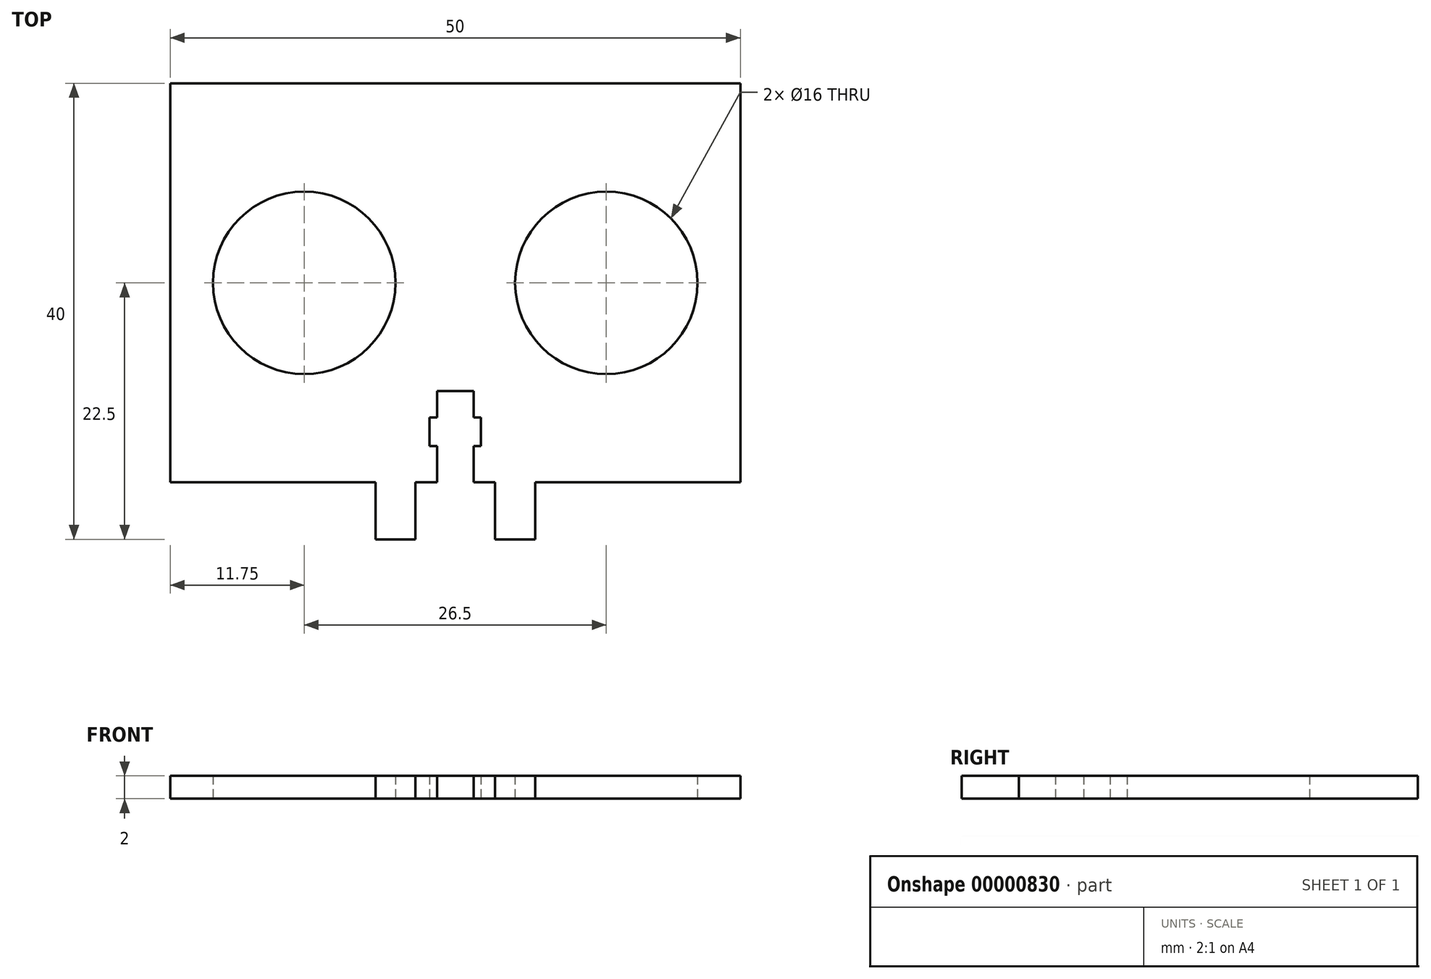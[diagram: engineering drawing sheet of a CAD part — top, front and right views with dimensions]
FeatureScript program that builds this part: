
annotation { "Feature Type Name" : "Feature", "Feature Type Description" : "" }
export const myFeature = defineFeature(function(context is Context, id is Id, definition is map)
    precondition{}
    {
        {
            var Q0;
            Q0=qCreatedBy(makeId("Top.planeOp"),FACE);
            var sketch = newSketch(context, id + "F0", { "sketchPlane" : qUnion([Q0])});
            skLineSegment(sketch, "E0.rect.bottom", {"start": v(25, -17.5) * mm, "end": v(1.6, -17.5) * mm});
            skLineSegment(sketch, "E0.rect.top", {"start": v(25, 17.5) * mm, "end": v(-25, 17.5) * mm});
            skLineSegment(sketch, "E0.rect.left", {"start": v(25, -17.5) * mm, "end": v(25, 17.5) * mm});
            skLineSegment(sketch, "E0.rect.right", {"start": v(-25, -17.5) * mm, "end": v(-25, 17.5) * mm});
            skPoint(sketch, "E0.rect.middle", {"position": v(0, 0) * mm});
            skLineSegment(sketch, "E1", {"start": v(-29.94, 0) * mm, "end": v(40.04, 0) * mm, "construction": true});
            skCircle(sketch, "E2", {"center": v(-13.25, 0) * mm, "radius": 8 * mm});
            skLineSegment(sketch, "E3", {"start": v(0, 12.7) * mm, "end": v(0, -27.18) * mm, "construction": true});
            skCircle(sketch, "E4.0.MirrorC", {"center": v(13.25, 0) * mm, "radius": 8 * mm});
            skLineSegment(sketch, "E5", {"start": v(-7, -17.5) * mm, "end": v(-7, -22.5) * mm});
            skLineSegment(sketch, "E6", {"start": v(-7, -22.5) * mm, "end": v(-3.5, -22.5) * mm});
            skLineSegment(sketch, "E7", {"start": v(-3.5, -22.5) * mm, "end": v(-3.5, -17.5) * mm});
            skLineSegment(sketch, "E8", {"start": v(-3.5, -17.5) * mm, "end": v(-1.6, -17.5) * mm});
            skLineSegment(sketch, "E9", {"start": v(-1.6, -17.5) * mm, "end": v(-1.6, -14.3) * mm});
            skLineSegment(sketch, "E10", {"start": v(-1.6, -14.3) * mm, "end": v(-2.25, -14.3) * mm});
            skLineSegment(sketch, "E11", {"start": v(-2.25, -14.3) * mm, "end": v(-2.25, -11.8) * mm});
            skLineSegment(sketch, "E12", {"start": v(-2.25, -11.8) * mm, "end": v(-1.6, -11.8) * mm});
            skLineSegment(sketch, "E13", {"start": v(-1.6, -11.8) * mm, "end": v(-1.6, -9.5) * mm});
            skLineSegment(sketch, "E14", {"start": v(-1.6, -9.5) * mm, "end": v(0, -9.5) * mm});
            skLineSegment(sketch, "E15.0.MirrorCS", {"start": v(2.25, -11.8) * mm, "end": v(1.6, -11.8) * mm});
            skLineSegment(sketch, "E15.1.MirrorCS", {"start": v(1.6, -14.3) * mm, "end": v(2.25, -14.3) * mm});
            skLineSegment(sketch, "E15.2.MirrorCS", {"start": v(7, -17.5) * mm, "end": v(7, -22.5) * mm});
            skLineSegment(sketch, "E15.3.MirrorCS", {"start": v(3.5, -22.5) * mm, "end": v(3.5, -17.5) * mm});
            skLineSegment(sketch, "E15.4.MirrorCS", {"start": v(7, -22.5) * mm, "end": v(3.5, -22.5) * mm});
            skLineSegment(sketch, "E15.5.MirrorCS", {"start": v(1.6, -17.5) * mm, "end": v(1.6, -14.3) * mm});
            skLineSegment(sketch, "E15.6.MirrorCS", {"start": v(1.6, -9.5) * mm, "end": v(0, -9.5) * mm});
            skLineSegment(sketch, "E15.7.MirrorCS", {"start": v(3.5, -17.5) * mm, "end": v(1.6, -17.5) * mm});
            skLineSegment(sketch, "E15.8.MirrorCS", {"start": v(1.6, -11.8) * mm, "end": v(1.6, -9.5) * mm});
            skLineSegment(sketch, "E15.9.MirrorCS", {"start": v(2.25, -14.3) * mm, "end": v(2.25, -11.8) * mm});
            skLineSegment(sketch, "E16.trimOffspring", {"start": v(-1.6, -17.5) * mm, "end": v(-25, -17.5) * mm});
            skSolve(sketch);
        }
        {
            var Q0;
            Q0 = qSketchRegion(id + "F0", true);
            extrude(context, id + "F1", {"entities" : qUnion([Q0]), "depth" : 2 * mm});
        }
    });
